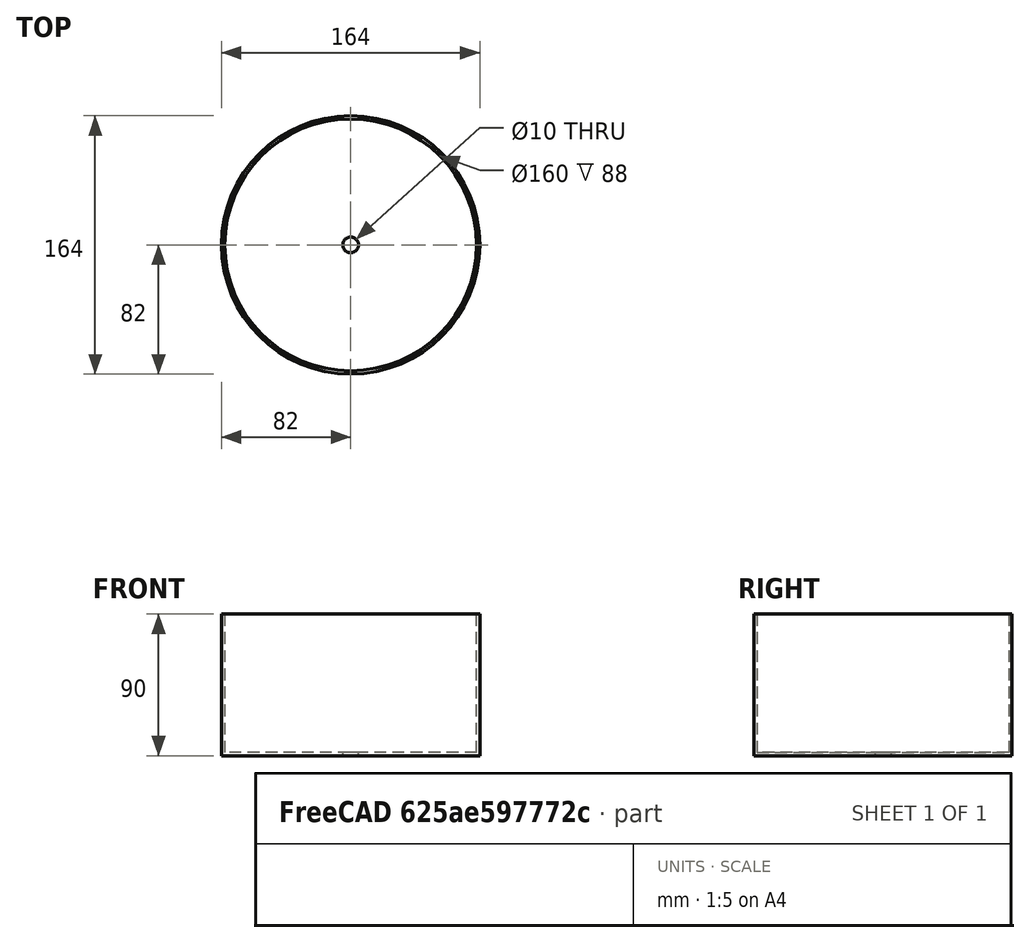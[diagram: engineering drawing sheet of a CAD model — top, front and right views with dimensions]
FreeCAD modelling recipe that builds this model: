
FCSTD DOCUMENT  (FreeCAD 0.19R)
Label: Pot
License: All rights reserved
LicenseURL: http://en.wikipedia.org/wiki/All_rights_reserved
objects: Sketcher::SketchObject×3, PartDesign::Pad×2, Mesh::Feature×1, PartDesign::Pocket×1, PartDesign::Body×1
note: 10 computed .brp shape members not serialized (recipe doc carries the construction recipe); baked Part::Feature solids carry a one-line shape summary decoded from their .brp

FEATURE [Mesh::Feature] TatoCageB2____v2
FEATURE [Sketcher::SketchObject] Sketch
  FullyConstrained = true
  MapMode = 5
  Support = -> [XY_Plane]
  sketch-geometry (2):
    g0: Circle CenterX=0 CenterY=0 CenterZ=0 NormalX=0 NormalY=0 NormalZ=1 AngleXU=0 Radius=80
    g1: Circle CenterX=0 CenterY=0 CenterZ=0 NormalX=0 NormalY=0 NormalZ=1 AngleXU=0 Radius=82
  constraints (4):
    c: Coincident(g0,g-1)
    c: Coincident(g1,g0)
    c: Radius(g0) = 80
    c: Radius(g1) = 82
FEATURE [PartDesign::Pad] Pad
  Direction = (1,1,1)
  Length = 90
  Length2 = 100
  Profile = -> Sketch
  Type = 0
FEATURE [Sketcher::SketchObject] Sketch001
  FullyConstrained = true
  MapMode = 5
  Support = -> [XY_Plane]
  sketch-geometry (1):
    g0: Circle CenterX=0 CenterY=0 CenterZ=0 NormalX=0 NormalY=0 NormalZ=1 AngleXU=0 Radius=82
  constraints (2):
    c: Coincident(g0,g-1)
    c: Radius(g0) = 82
FEATURE [PartDesign::Pad] Pad001
  BaseFeature = -> Pad
  Direction = (1,1,1)
  Length = 2
  Length2 = 100
  Profile = -> Sketch001
  Type = 0
FEATURE [Sketcher::SketchObject] Sketch002
  FullyConstrained = true
  MapMode = 5
  Support = -> [XY_Plane]
  sketch-geometry (1):
    g0: Circle CenterX=0 CenterY=0 CenterZ=0 NormalX=0 NormalY=0 NormalZ=1 AngleXU=0 Radius=5
  constraints (2):
    c: Coincident(g0,g-1)
    c: Radius(g0) = 5
FEATURE [PartDesign::Pocket] Pocket
  BaseFeature = -> Pad001
  Length = 5
  Length2 = 100
  Profile = -> Sketch002
  Reversed = true
  Type = 0
FEATURE [PartDesign::Body] Body
  Group = -> [Sketch,Pad,Sketch001,Pad001,Sketch002,Pocket]
  Origin = -> Origin
  Tip = -> Pocket
